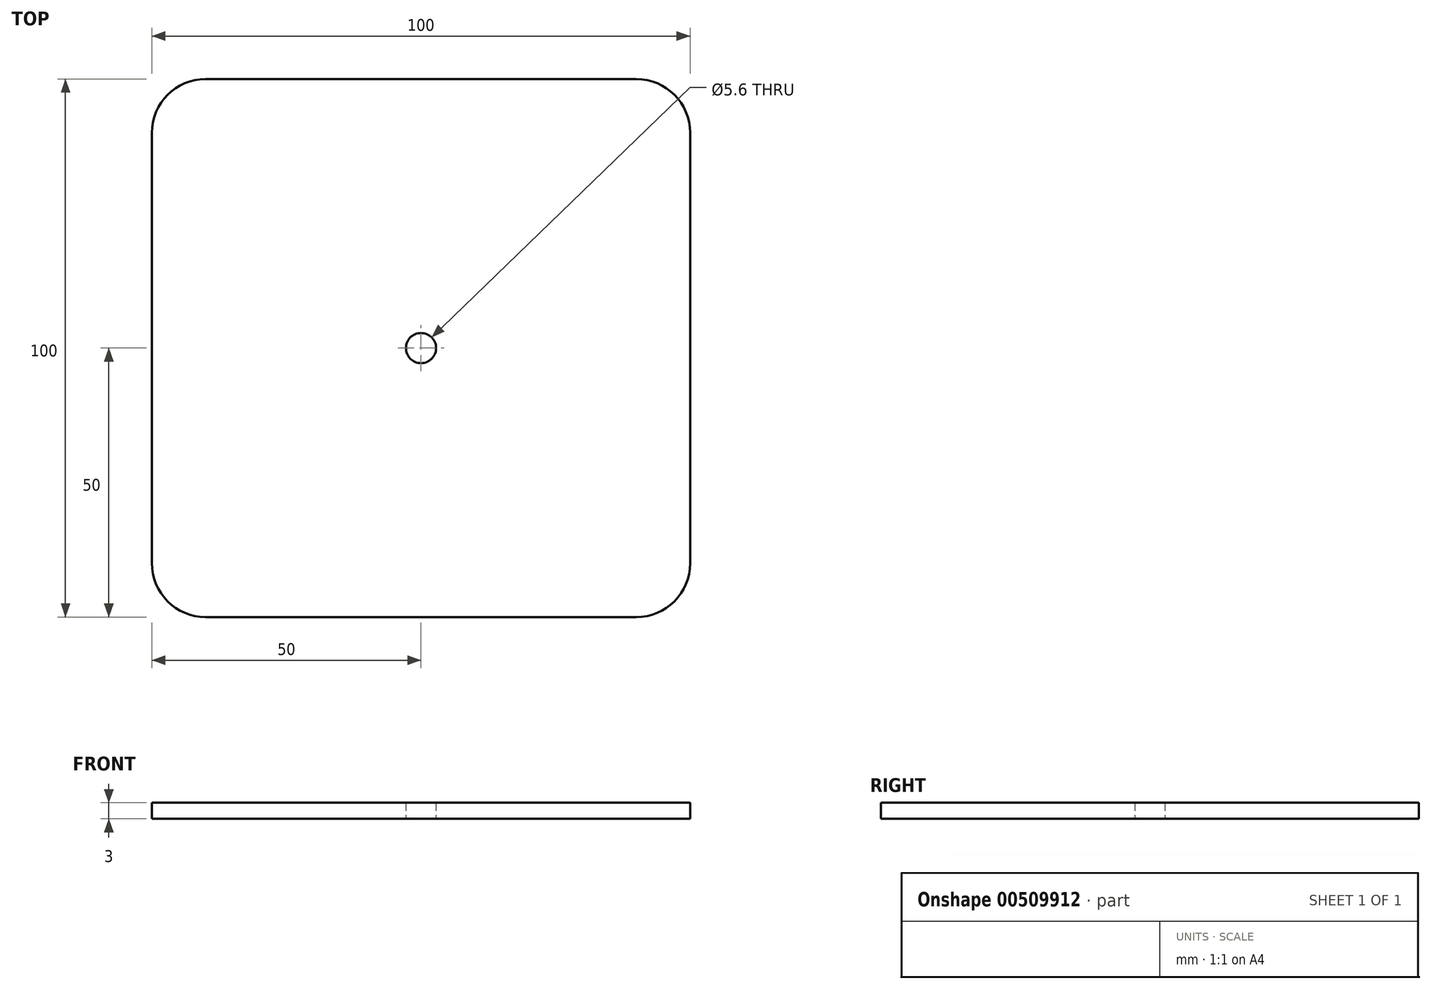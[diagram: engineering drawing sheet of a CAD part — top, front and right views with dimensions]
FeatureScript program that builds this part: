
annotation { "Feature Type Name" : "Feature", "Feature Type Description" : "" }
export const myFeature = defineFeature(function(context is Context, id is Id, definition is map)
    precondition{}
    {
        {
            var Q0;
            Q0=qCreatedBy(makeId("Top.planeOp"),FACE);
            var sketch = newSketch(context, id + "F0", { "sketchPlane" : qUnion([Q0])});
            skLineSegment(sketch, "E0.bottom", {"start": v(50, 50) * mm, "end": v(-50, 50) * mm});
            skLineSegment(sketch, "E0.top", {"start": v(50, -50) * mm, "end": v(-50, -50) * mm});
            skLineSegment(sketch, "E0.left", {"start": v(50, 50) * mm, "end": v(50, -50) * mm});
            skLineSegment(sketch, "E0.right", {"start": v(-50, 50) * mm, "end": v(-50, -50) * mm});
            skPoint(sketch, "E0.middle", {"position": v(0, 0) * mm});
            skCircle(sketch, "E1", {"center": v(0, 0) * mm, "radius": 2.8 * mm});
            skSolve(sketch);
        }
        {
            var Q0;
            Q0=makeQuery(id+"F0.imprint","IMPRINT",FACE,{"disambiguationData":[TD([[makeQuery(id+"F0.imprint","IMPRINT",EDGE,{"derivedFrom":sQuery(id+"F0.wireOp",EDGE,"E0.bottom")}),1.0]])]});
            extrude(context, id + "F1", {"entities" : qUnion([Q0]), "depth" : 3 * mm});
        }
        {
            var Q0;
            Q0=makeQuery(id+"F1.opExtrude","SWEPT_EDGE",EDGE,{"disambiguationData":[OSD([sQuery(id+"F0.wireOp",EDGE,"E0.top"),sQuery(id+"F0.wireOp",EDGE,"E0.left")])]});
            var Q1;
            Q1=makeQuery(id+"F1.opExtrude","SWEPT_EDGE",EDGE,{"disambiguationData":[OSD([sQuery(id+"F0.wireOp",EDGE,"E0.bottom"),sQuery(id+"F0.wireOp",EDGE,"E0.left")])]});
            var Q2;
            Q2=makeQuery(id+"F1.opExtrude","SWEPT_EDGE",EDGE,{"disambiguationData":[OSD([sQuery(id+"F0.wireOp",EDGE,"E0.top"),sQuery(id+"F0.wireOp",EDGE,"E0.right")])]});
            var Q3;
            Q3=makeQuery(id+"F1.opExtrude","SWEPT_EDGE",EDGE,{"disambiguationData":[OSD([sQuery(id+"F0.wireOp",EDGE,"E0.bottom"),sQuery(id+"F0.wireOp",EDGE,"E0.right")])]});
            fillet(context, id + "F2", {"entities" : qUnion([Q0, Q1, Q2, Q3]), "radius" : 10 * mm, "tangentPropagation" : true, "allowEdgeOverflow" : false});
        }
    });
